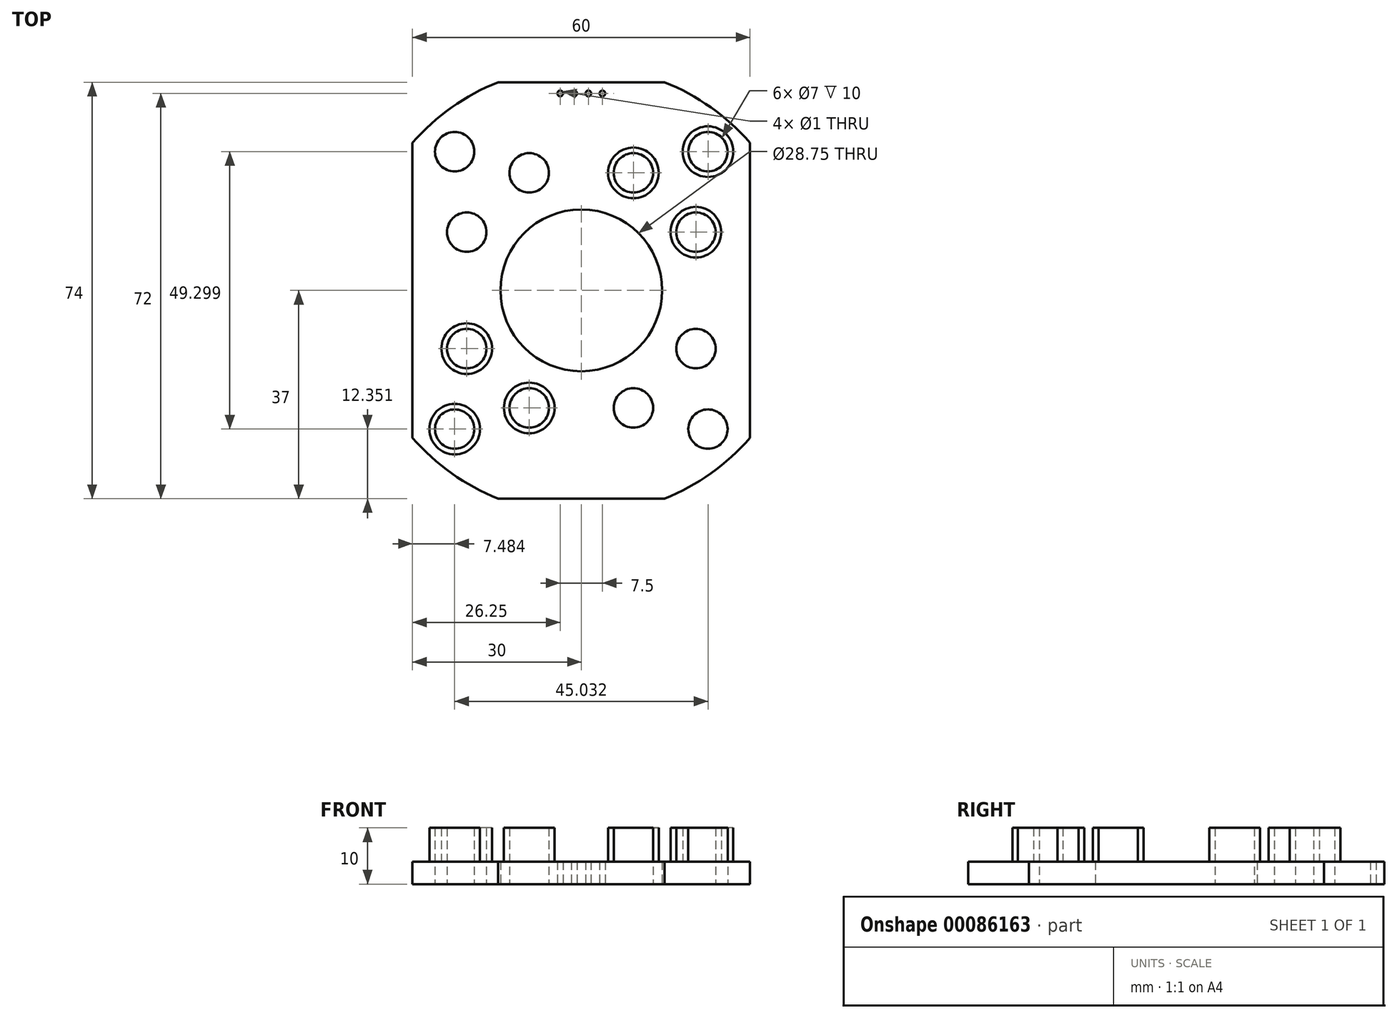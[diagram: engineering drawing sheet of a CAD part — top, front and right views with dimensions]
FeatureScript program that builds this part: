
annotation { "Feature Type Name" : "Feature", "Feature Type Description" : "" }
export const myFeature = defineFeature(function(context is Context, id is Id, definition is map)
    precondition{}
    {
        {
            var Q0;
            Q0=qCreatedBy(makeId("Top.planeOp"),FACE);
            var sketch = newSketch(context, id + "F0", { "sketchPlane" : qUnion([Q0])});
            skLineSegment(sketch, "E0.bottom", {"start": v(-30, 37) * mm, "end": v(30, 37) * mm});
            skLineSegment(sketch, "E0.top", {"start": v(-30, -37) * mm, "end": v(30, -37) * mm});
            skLineSegment(sketch, "E0.left", {"start": v(-30, 37) * mm, "end": v(-30, -37) * mm});
            skLineSegment(sketch, "E0.right", {"start": v(30, 37) * mm, "end": v(30, -37) * mm});
            skPoint(sketch, "E0.middle", {"position": v(0, 0) * mm});
            skCircle(sketch, "E1", {"center": v(0, 0) * mm, "radius": 14.37 * mm});
            skCircle(sketch, "E2", {"center": v(0, 0) * mm, "radius": 39.85 * mm});
            skCircle(sketch, "E3", {"center": v(-3.75, 35) * mm, "radius": 0.5 * mm});
            skCircle(sketch, "E4.1.0.0", {"center": v(-1.25, 35) * mm, "radius": 0.5 * mm});
            skCircle(sketch, "E4.2.0.0", {"center": v(1.25, 35) * mm, "radius": 0.5 * mm});
            skLineSegment(sketch, "E4.direction1", {"start": v(-3.75, 35) * mm, "end": v(-1.25, 35) * mm, "construction": true});
            skCircle(sketch, "E5.0.3.0", {"center": v(3.75, 35) * mm, "radius": 0.5 * mm});
            skCircle(sketch, "E6", {"center": v(0, 0) * mm, "radius": 22.85 * mm, "construction": true});
            skCircle(sketch, "E7", {"center": v(0, 0) * mm, "radius": 33.38 * mm, "construction": true});
            skCircle(sketch, "E8", {"center": v(-22.52, 24.65) * mm, "radius": 4.5 * mm});
            skCircle(sketch, "E9", {"center": v(-9.26, 20.89) * mm, "radius": 4.5 * mm});
            skCircle(sketch, "E10", {"center": v(-20.37, 10.35) * mm, "radius": 4.5 * mm});
            skCircle(sketch, "E11.MirrorC", {"center": v(22.52, 24.65) * mm, "radius": 4.5 * mm});
            skCircle(sketch, "E12.MirrorC", {"center": v(20.37, 10.35) * mm, "radius": 4.5 * mm});
            skCircle(sketch, "E13.MirrorC", {"center": v(9.26, 20.89) * mm, "radius": 4.5 * mm});
            skCircle(sketch, "E14.MirrorC", {"center": v(22.52, -24.65) * mm, "radius": 4.5 * mm});
            skCircle(sketch, "E15.MirrorC", {"center": v(-22.52, -24.65) * mm, "radius": 4.5 * mm});
            skCircle(sketch, "E16.MirrorC", {"center": v(-20.37, -10.35) * mm, "radius": 4.5 * mm});
            skCircle(sketch, "E17.MirrorC", {"center": v(-9.26, -20.89) * mm, "radius": 4.5 * mm});
            skCircle(sketch, "E18.MirrorC", {"center": v(9.26, -20.89) * mm, "radius": 4.5 * mm});
            skCircle(sketch, "E19.MirrorC", {"center": v(20.37, -10.35) * mm, "radius": 4.5 * mm});
            skCircle(sketch, "E20", {"center": v(-22.52, 24.65) * mm, "radius": 3.5 * mm});
            skCircle(sketch, "E21", {"center": v(-9.26, 20.89) * mm, "radius": 3.5 * mm});
            skCircle(sketch, "E22", {"center": v(-20.37, 10.35) * mm, "radius": 3.5 * mm});
            skCircle(sketch, "E23.MirrorC", {"center": v(22.52, 24.65) * mm, "radius": 3.5 * mm});
            skCircle(sketch, "E24.MirrorC", {"center": v(9.26, 20.89) * mm, "radius": 3.5 * mm});
            skCircle(sketch, "E25.MirrorC", {"center": v(20.37, 10.35) * mm, "radius": 3.5 * mm});
            skCircle(sketch, "E26.MirrorC", {"center": v(-20.37, -10.35) * mm, "radius": 3.5 * mm});
            skCircle(sketch, "E27.MirrorC", {"center": v(-22.52, -24.65) * mm, "radius": 3.5 * mm});
            skCircle(sketch, "E28.MirrorC", {"center": v(-9.26, -20.89) * mm, "radius": 3.5 * mm});
            skCircle(sketch, "E29.MirrorC", {"center": v(9.26, -20.89) * mm, "radius": 3.5 * mm});
            skCircle(sketch, "E30.MirrorC", {"center": v(20.37, -10.35) * mm, "radius": 3.5 * mm});
            skCircle(sketch, "E31.MirrorC", {"center": v(22.52, -24.65) * mm, "radius": 3.5 * mm});
            skSolve(sketch);
        }
        {
            var Q0;
            Q0=makeQuery(id+"F0.imprint","IMPRINT",FACE,{"disambiguationData":[TD([[makeQuery(id+"F0.imprint","IMPRINT",EDGE,{"derivedFrom":sQuery(id+"F0.wireOp",EDGE,"E1")}),-1.0]])]});
            var Q1;
            Q1=makeQuery(id+"F0.imprint","IMPRINT",FACE,{"disambiguationData":[TD([[makeQuery(id+"F0.imprint","IMPRINT",EDGE,{"derivedFrom":sQuery(id+"F0.wireOp",EDGE,"E20")}),1.0]])]});
            var Q2;
            Q2=makeQuery(id+"F0.imprint","IMPRINT",FACE,{"disambiguationData":[TD([[makeQuery(id+"F0.imprint","IMPRINT",EDGE,{"derivedFrom":sQuery(id+"F0.wireOp",EDGE,"E21")}),1.0]])]});
            var Q3;
            Q3=makeQuery(id+"F0.imprint","IMPRINT",FACE,{"disambiguationData":[TD([[makeQuery(id+"F0.imprint","IMPRINT",EDGE,{"derivedFrom":sQuery(id+"F0.wireOp",EDGE,"E24.MirrorC")}),-1.0]])]});
            var Q4;
            Q4=makeQuery(id+"F0.imprint","IMPRINT",FACE,{"disambiguationData":[TD([[makeQuery(id+"F0.imprint","IMPRINT",EDGE,{"derivedFrom":sQuery(id+"F0.wireOp",EDGE,"E25.MirrorC")}),-1.0]])]});
            var Q5;
            Q5=makeQuery(id+"F0.imprint","IMPRINT",FACE,{"disambiguationData":[TD([[makeQuery(id+"F0.imprint","IMPRINT",EDGE,{"derivedFrom":sQuery(id+"F0.wireOp",EDGE,"E30.MirrorC")}),1.0]])]});
            var Q6;
            Q6=makeQuery(id+"F0.imprint","IMPRINT",FACE,{"disambiguationData":[TD([[makeQuery(id+"F0.imprint","IMPRINT",EDGE,{"derivedFrom":sQuery(id+"F0.wireOp",EDGE,"E23.MirrorC")}),-1.0]])]});
            var Q7;
            Q7=makeQuery(id+"F0.imprint","IMPRINT",FACE,{"disambiguationData":[TD([[makeQuery(id+"F0.imprint","IMPRINT",EDGE,{"derivedFrom":sQuery(id+"F0.wireOp",EDGE,"E29.MirrorC")}),1.0]])]});
            var Q8;
            Q8=makeQuery(id+"F0.imprint","IMPRINT",FACE,{"disambiguationData":[TD([[makeQuery(id+"F0.imprint","IMPRINT",EDGE,{"derivedFrom":sQuery(id+"F0.wireOp",EDGE,"E31.MirrorC")}),1.0]])]});
            var Q9;
            Q9=makeQuery(id+"F0.imprint","IMPRINT",FACE,{"disambiguationData":[TD([[makeQuery(id+"F0.imprint","IMPRINT",EDGE,{"derivedFrom":sQuery(id+"F0.wireOp",EDGE,"E28.MirrorC")}),-1.0]])]});
            var Q10;
            Q10=makeQuery(id+"F0.imprint","IMPRINT",FACE,{"disambiguationData":[TD([[makeQuery(id+"F0.imprint","IMPRINT",EDGE,{"derivedFrom":sQuery(id+"F0.wireOp",EDGE,"E26.MirrorC")}),-1.0]])]});
            var Q11;
            Q11=makeQuery(id+"F0.imprint","IMPRINT",FACE,{"disambiguationData":[TD([[makeQuery(id+"F0.imprint","IMPRINT",EDGE,{"derivedFrom":sQuery(id+"F0.wireOp",EDGE,"E22")}),1.0]])]});
            var Q12;
            Q12=makeQuery(id+"F0.imprint","IMPRINT",FACE,{"disambiguationData":[TD([[makeQuery(id+"F0.imprint","IMPRINT",EDGE,{"derivedFrom":sQuery(id+"F0.wireOp",EDGE,"E27.MirrorC")}),-1.0]])]});
            var Q13;
            Q13=makeQuery(id+"F0.imprint","IMPRINT",FACE,{"disambiguationData":[TD([[makeQuery(id+"F0.imprint","IMPRINT",EDGE,{"derivedFrom":sQuery(id+"F0.wireOp",EDGE,"E15.MirrorC")}),-1.0]])]});
            var Q14;
            Q14=makeQuery(id+"F0.imprint","IMPRINT",FACE,{"disambiguationData":[TD([[makeQuery(id+"F0.imprint","IMPRINT",EDGE,{"derivedFrom":sQuery(id+"F0.wireOp",EDGE,"E17.MirrorC")}),-1.0]])]});
            var Q15;
            Q15=makeQuery(id+"F0.imprint","IMPRINT",FACE,{"disambiguationData":[TD([[makeQuery(id+"F0.imprint","IMPRINT",EDGE,{"derivedFrom":sQuery(id+"F0.wireOp",EDGE,"E16.MirrorC")}),-1.0]])]});
            var Q16;
            Q16=makeQuery(id+"F0.imprint","IMPRINT",FACE,{"disambiguationData":[TD([[makeQuery(id+"F0.imprint","IMPRINT",EDGE,{"derivedFrom":sQuery(id+"F0.wireOp",EDGE,"E10")}),1.0]])]});
            var Q17;
            Q17=makeQuery(id+"F0.imprint","IMPRINT",FACE,{"disambiguationData":[TD([[makeQuery(id+"F0.imprint","IMPRINT",EDGE,{"derivedFrom":sQuery(id+"F0.wireOp",EDGE,"E8")}),1.0]])]});
            var Q18;
            Q18=makeQuery(id+"F0.imprint","IMPRINT",FACE,{"disambiguationData":[TD([[makeQuery(id+"F0.imprint","IMPRINT",EDGE,{"derivedFrom":sQuery(id+"F0.wireOp",EDGE,"E9")}),1.0]])]});
            var Q19;
            Q19=makeQuery(id+"F0.imprint","IMPRINT",FACE,{"disambiguationData":[TD([[makeQuery(id+"F0.imprint","IMPRINT",EDGE,{"derivedFrom":sQuery(id+"F0.wireOp",EDGE,"E13.MirrorC")}),-1.0]])]});
            var Q20;
            Q20=makeQuery(id+"F0.imprint","IMPRINT",FACE,{"disambiguationData":[TD([[makeQuery(id+"F0.imprint","IMPRINT",EDGE,{"derivedFrom":sQuery(id+"F0.wireOp",EDGE,"E11.MirrorC")}),-1.0]])]});
            var Q21;
            Q21=makeQuery(id+"F0.imprint","IMPRINT",FACE,{"disambiguationData":[TD([[makeQuery(id+"F0.imprint","IMPRINT",EDGE,{"derivedFrom":sQuery(id+"F0.wireOp",EDGE,"E12.MirrorC")}),-1.0]])]});
            var Q22;
            Q22=makeQuery(id+"F0.imprint","IMPRINT",FACE,{"disambiguationData":[TD([[makeQuery(id+"F0.imprint","IMPRINT",EDGE,{"derivedFrom":sQuery(id+"F0.wireOp",EDGE,"E18.MirrorC")}),1.0]])]});
            var Q23;
            Q23=makeQuery(id+"F0.imprint","IMPRINT",FACE,{"disambiguationData":[TD([[makeQuery(id+"F0.imprint","IMPRINT",EDGE,{"derivedFrom":sQuery(id+"F0.wireOp",EDGE,"E14.MirrorC")}),1.0]])]});
            var Q24;
            Q24=makeQuery(id+"F0.imprint","IMPRINT",FACE,{"disambiguationData":[TD([[makeQuery(id+"F0.imprint","IMPRINT",EDGE,{"derivedFrom":sQuery(id+"F0.wireOp",EDGE,"E19.MirrorC")}),1.0]])]});
            extrude(context, id + "F1", {"entities" : qUnion([Q0, Q1, Q2, Q3, Q4, Q5, Q6, Q7, Q8, Q9, Q10, Q11, Q12, Q13, Q14, Q15, Q16, Q17, Q18, Q19, Q20, Q21, Q22, Q23, Q24]), "depth" : 2 * mm});
        }
        {
            var Q0;
            Q0=makeQuery(id+"F0.imprint","IMPRINT",FACE,{"disambiguationData":[TD([[makeQuery(id+"F0.imprint","IMPRINT",EDGE,{"derivedFrom":sQuery(id+"F0.wireOp",EDGE,"E8")}),1.0]])]});
            var Q1;
            Q1=makeQuery(id+"F0.imprint","IMPRINT",FACE,{"disambiguationData":[TD([[makeQuery(id+"F0.imprint","IMPRINT",EDGE,{"derivedFrom":sQuery(id+"F0.wireOp",EDGE,"E9")}),1.0]])]});
            var Q2;
            Q2=makeQuery(id+"F0.imprint","IMPRINT",FACE,{"disambiguationData":[TD([[makeQuery(id+"F0.imprint","IMPRINT",EDGE,{"derivedFrom":sQuery(id+"F0.wireOp",EDGE,"E10")}),1.0]])]});
            var Q3;
            Q3=makeQuery(id+"F0.imprint","IMPRINT",FACE,{"disambiguationData":[TD([[makeQuery(id+"F0.imprint","IMPRINT",EDGE,{"derivedFrom":sQuery(id+"F0.wireOp",EDGE,"E13.MirrorC")}),-1.0]])]});
            var Q4;
            Q4=makeQuery(id+"F0.imprint","IMPRINT",FACE,{"disambiguationData":[TD([[makeQuery(id+"F0.imprint","IMPRINT",EDGE,{"derivedFrom":sQuery(id+"F0.wireOp",EDGE,"E12.MirrorC")}),-1.0]])]});
            var Q5;
            Q5=makeQuery(id+"F0.imprint","IMPRINT",FACE,{"disambiguationData":[TD([[makeQuery(id+"F0.imprint","IMPRINT",EDGE,{"derivedFrom":sQuery(id+"F0.wireOp",EDGE,"E11.MirrorC")}),-1.0]])]});
            var Q6;
            Q6=makeQuery(id+"F0.imprint","IMPRINT",FACE,{"disambiguationData":[TD([[makeQuery(id+"F0.imprint","IMPRINT",EDGE,{"derivedFrom":sQuery(id+"F0.wireOp",EDGE,"E19.MirrorC")}),1.0]])]});
            var Q7;
            Q7=makeQuery(id+"F0.imprint","IMPRINT",FACE,{"disambiguationData":[TD([[makeQuery(id+"F0.imprint","IMPRINT",EDGE,{"derivedFrom":sQuery(id+"F0.wireOp",EDGE,"E18.MirrorC")}),1.0]])]});
            var Q8;
            Q8=makeQuery(id+"F0.imprint","IMPRINT",FACE,{"disambiguationData":[TD([[makeQuery(id+"F0.imprint","IMPRINT",EDGE,{"derivedFrom":sQuery(id+"F0.wireOp",EDGE,"E14.MirrorC")}),1.0]])]});
            var Q9;
            Q9=makeQuery(id+"F0.imprint","IMPRINT",FACE,{"disambiguationData":[TD([[makeQuery(id+"F0.imprint","IMPRINT",EDGE,{"derivedFrom":sQuery(id+"F0.wireOp",EDGE,"E15.MirrorC")}),-1.0]])]});
            var Q10;
            Q10=makeQuery(id+"F0.imprint","IMPRINT",FACE,{"disambiguationData":[TD([[makeQuery(id+"F0.imprint","IMPRINT",EDGE,{"derivedFrom":sQuery(id+"F0.wireOp",EDGE,"E17.MirrorC")}),-1.0]])]});
            var Q11;
            Q11=makeQuery(id+"F0.imprint","IMPRINT",FACE,{"disambiguationData":[TD([[makeQuery(id+"F0.imprint","IMPRINT",EDGE,{"derivedFrom":sQuery(id+"F0.wireOp",EDGE,"E16.MirrorC")}),-1.0]])]});
            extrude(context, id + "F2", {"entities" : qUnion([Q0, Q1, Q2, Q3, Q4, Q5, Q6, Q7, Q8, Q9, Q10, Q11]), "operationType" : NewBodyOperationType.ADD, "depth" : 4 * mm});
        }
        {
            var Q0;
            Q0=makeQuery(id+"F0.imprint","IMPRINT",FACE,{"disambiguationData":[TD([[makeQuery(id+"F0.imprint","IMPRINT",EDGE,{"derivedFrom":sQuery(id+"F0.wireOp",EDGE,"E20")}),1.0]])]});
            var Q1;
            Q1=makeQuery(id+"F0.imprint","IMPRINT",FACE,{"disambiguationData":[TD([[makeQuery(id+"F0.imprint","IMPRINT",EDGE,{"derivedFrom":sQuery(id+"F0.wireOp",EDGE,"E22")}),1.0]])]});
            var Q2;
            Q2=makeQuery(id+"F0.imprint","IMPRINT",FACE,{"disambiguationData":[TD([[makeQuery(id+"F0.imprint","IMPRINT",EDGE,{"derivedFrom":sQuery(id+"F0.wireOp",EDGE,"E21")}),1.0]])]});
            var Q3;
            Q3=makeQuery(id+"F0.imprint","IMPRINT",FACE,{"disambiguationData":[TD([[makeQuery(id+"F0.imprint","IMPRINT",EDGE,{"derivedFrom":sQuery(id+"F0.wireOp",EDGE,"E24.MirrorC")}),-1.0]])]});
            var Q4;
            Q4=makeQuery(id+"F0.imprint","IMPRINT",FACE,{"disambiguationData":[TD([[makeQuery(id+"F0.imprint","IMPRINT",EDGE,{"derivedFrom":sQuery(id+"F0.wireOp",EDGE,"E23.MirrorC")}),-1.0]])]});
            var Q5;
            Q5=makeQuery(id+"F0.imprint","IMPRINT",FACE,{"disambiguationData":[TD([[makeQuery(id+"F0.imprint","IMPRINT",EDGE,{"derivedFrom":sQuery(id+"F0.wireOp",EDGE,"E25.MirrorC")}),-1.0]])]});
            var Q6;
            Q6=makeQuery(id+"F0.imprint","IMPRINT",FACE,{"disambiguationData":[TD([[makeQuery(id+"F0.imprint","IMPRINT",EDGE,{"derivedFrom":sQuery(id+"F0.wireOp",EDGE,"E30.MirrorC")}),1.0]])]});
            var Q7;
            Q7=makeQuery(id+"F0.imprint","IMPRINT",FACE,{"disambiguationData":[TD([[makeQuery(id+"F0.imprint","IMPRINT",EDGE,{"derivedFrom":sQuery(id+"F0.wireOp",EDGE,"E31.MirrorC")}),1.0]])]});
            var Q8;
            Q8=makeQuery(id+"F0.imprint","IMPRINT",FACE,{"disambiguationData":[TD([[makeQuery(id+"F0.imprint","IMPRINT",EDGE,{"derivedFrom":sQuery(id+"F0.wireOp",EDGE,"E29.MirrorC")}),1.0]])]});
            var Q9;
            Q9=makeQuery(id+"F0.imprint","IMPRINT",FACE,{"disambiguationData":[TD([[makeQuery(id+"F0.imprint","IMPRINT",EDGE,{"derivedFrom":sQuery(id+"F0.wireOp",EDGE,"E28.MirrorC")}),-1.0]])]});
            var Q10;
            Q10=makeQuery(id+"F0.imprint","IMPRINT",FACE,{"disambiguationData":[TD([[makeQuery(id+"F0.imprint","IMPRINT",EDGE,{"derivedFrom":sQuery(id+"F0.wireOp",EDGE,"E26.MirrorC")}),-1.0]])]});
            var Q11;
            Q11=makeQuery(id+"F0.imprint","IMPRINT",FACE,{"disambiguationData":[TD([[makeQuery(id+"F0.imprint","IMPRINT",EDGE,{"derivedFrom":sQuery(id+"F0.wireOp",EDGE,"E27.MirrorC")}),-1.0]])]});
            extrude(context, id + "F3", {"entities" : qUnion([Q0, Q1, Q2, Q3, Q4, Q5, Q6, Q7, Q8, Q9, Q10, Q11]), "operationType" : NewBodyOperationType.ADD, "depth" : 10 * mm});
        }
    });
